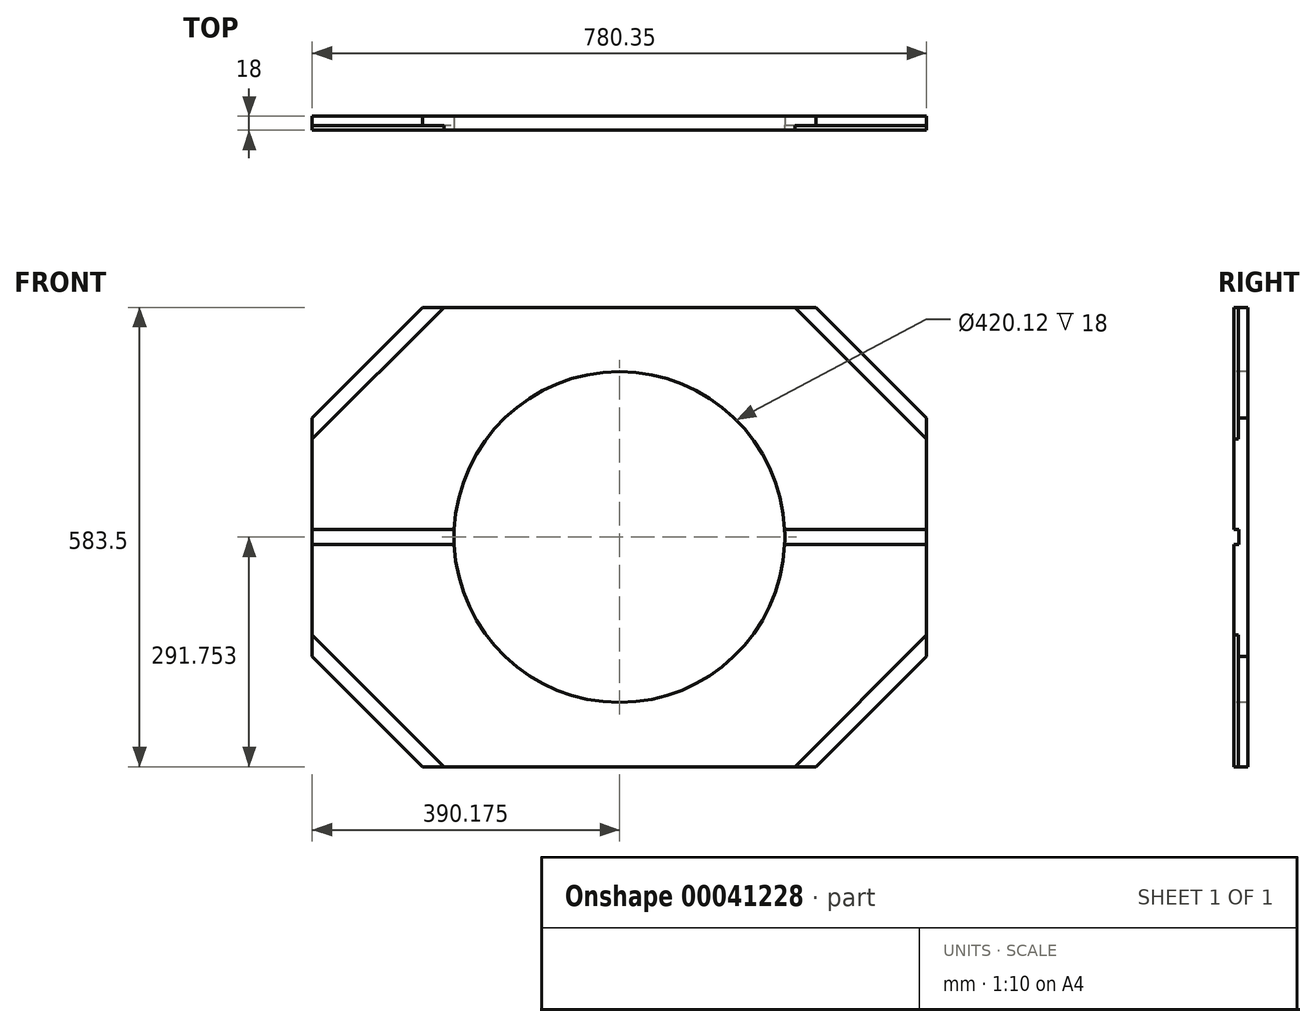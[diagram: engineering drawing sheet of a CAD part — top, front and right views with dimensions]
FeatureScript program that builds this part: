
annotation { "Feature Type Name" : "Feature", "Feature Type Description" : "" }
export const myFeature = defineFeature(function(context is Context, id is Id, definition is map)
    precondition{}
    {
        {
            var Q0;
            Q0=qCreatedBy(makeId("Front.planeOp"),FACE);
            var sketch = newSketch(context, id + "F0", { "sketchPlane" : qUnion([Q0])});
            skLineSegment(sketch, "E0.bottom", {"start": v(-320.85, 288.5) * mm, "end": v(459.5, 288.5) * mm});
            skLineSegment(sketch, "E0.top", {"start": v(-320.85, -295) * mm, "end": v(459.5, -295) * mm});
            skLineSegment(sketch, "E0.left", {"start": v(-320.85, 288.5) * mm, "end": v(-320.85, -295) * mm});
            skLineSegment(sketch, "E0.right", {"start": v(459.5, 288.5) * mm, "end": v(459.5, -295) * mm});
            skSolve(sketch);
        }
        {
            var Q0;
            Q0 = qSketchRegion(id + "F0", true);
            extrude(context, id + "F1", {"entities" : qUnion([Q0]), "depth" : 18 * mm});
        }
        {
            var Q0;
            Q0=makeQuery(id+"F1.opExtrude","CAP_FACE",FACE,{"disambiguationData":[OSD([sQuery(id+"F0.wireOp",EDGE,"E0.bottom"),sQuery(id+"F0.wireOp",EDGE,"E0.top"),sQuery(id+"F0.wireOp",EDGE,"E0.left"),sQuery(id+"F0.wireOp",EDGE,"E0.right")])],"isStart":false});
            var sketch = newSketch(context, id + "F2", { "sketchPlane" : qUnion([Q0])});
            skLineSegment(sketch, "E1", {"start": v(-320.85, -3.25) * mm, "end": v(459.5, -3.25) * mm, "construction": true});
            skLineSegment(sketch, "E2", {"start": v(69.32, -295) * mm, "end": v(69.32, 288.5) * mm, "construction": true});
            skPoint(sketch, "E3", {"position": v(69.32, -3.25) * mm});
            skSolve(sketch);
        }
        {
            var Q0;
            Q0=sQuery(id+"F2.wireOp",VERTEX,"E3");
            var Q1;
            Q1=makeQuery(id+"F1.opExtrude","SWEPT_BODY",BODY,{"disambiguationData":[OSD([sQuery(id+"F0.wireOp",EDGE,"E0.bottom"),sQuery(id+"F0.wireOp",EDGE,"E0.top"),sQuery(id+"F0.wireOp",EDGE,"E0.left"),sQuery(id+"F0.wireOp",EDGE,"E0.right")])]});
            hole(context, id + "F3", {"style" : HoleStyle.SIMPLE, "holeDiameter" : 420.12 * mm, "endStyle" : HoleEndStyle.THROUGH, "locations" : qUnion([Q0]), "scope" : qUnion([Q1])});
        }
        {
            var Q0;
            Q0=makeQuery(id+"F1.opExtrude","CAP_FACE",FACE,{"disambiguationData":[OSD([sQuery(id+"F0.wireOp",EDGE,"E0.bottom"),sQuery(id+"F0.wireOp",EDGE,"E0.top"),sQuery(id+"F0.wireOp",EDGE,"E0.left"),sQuery(id+"F0.wireOp",EDGE,"E0.right")])],"isStart":false});
            var sketch = newSketch(context, id + "F4", { "sketchPlane" : qUnion([Q0])});
            skLineSegment(sketch, "E4", {"start": v(-320.85, -154.63) * mm, "end": v(-180.48, -295) * mm});
            skLineSegment(sketch, "E5", {"start": v(-320.85, -154.63) * mm, "end": v(-320.85, -295) * mm});
            skLineSegment(sketch, "E6", {"start": v(-320.85, -295) * mm, "end": v(-180.48, -295) * mm});
            skLineSegment(sketch, "E7", {"start": v(-320.85, 148.14) * mm, "end": v(-180.49, 288.5) * mm});
            skLineSegment(sketch, "E8", {"start": v(-180.49, 288.5) * mm, "end": v(-320.85, 288.5) * mm});
            skLineSegment(sketch, "E9", {"start": v(-320.85, 288.5) * mm, "end": v(-320.85, 148.14) * mm});
            skLineSegment(sketch, "E10", {"start": v(459.5, 288.5) * mm, "end": v(459.5, 148.14) * mm});
            skLineSegment(sketch, "E11", {"start": v(459.5, 148.14) * mm, "end": v(319.14, 288.5) * mm});
            skLineSegment(sketch, "E12", {"start": v(319.14, 288.5) * mm, "end": v(459.5, 288.5) * mm});
            skLineSegment(sketch, "E13", {"start": v(459.5, -154.64) * mm, "end": v(319.14, -295) * mm});
            skLineSegment(sketch, "E14", {"start": v(319.14, -295) * mm, "end": v(459.5, -295) * mm});
            skLineSegment(sketch, "E15", {"start": v(459.5, -295) * mm, "end": v(459.5, -154.64) * mm});
            skSolve(sketch);
        }
        {
            var Q0;
            Q0 = qSketchRegion(id + "F4", true);
            extrude(context, id + "F5", {"entities" : qUnion([Q0]), "operationType" : NewBodyOperationType.REMOVE, "endBound" : BoundingType.THROUGH_ALL, "oppositeDirection" : true, "depth" : 25.4 * mm});
        }
        {
            var Q0;
            Q0=makeQuery(id+"F1.opExtrude","CAP_FACE",FACE,{"disambiguationData":[OSD([sQuery(id+"F0.wireOp",EDGE,"E0.bottom"),sQuery(id+"F0.wireOp",EDGE,"E0.top"),sQuery(id+"F0.wireOp",EDGE,"E0.left"),sQuery(id+"F0.wireOp",EDGE,"E0.right")])],"isStart":false});
            var sketch = newSketch(context, id + "F6", { "sketchPlane" : qUnion([Q0])});
            skLineSegment(sketch, "E16", {"start": v(-320.85, -154.63) * mm, "end": v(-320.85, -127.76) * mm});
            skLineSegment(sketch, "E17", {"start": v(-320.85, -127.76) * mm, "end": v(-153.61, -295) * mm});
            skLineSegment(sketch, "E18", {"start": v(-153.61, -295) * mm, "end": v(-180.48, -295) * mm});
            skLineSegment(sketch, "E19", {"start": v(-180.48, -295) * mm, "end": v(-320.85, -154.63) * mm});
            skLineSegment(sketch, "E20", {"start": v(69.32, 288.5) * mm, "end": v(69.32, -295) * mm, "construction": true});
            skLineSegment(sketch, "E21", {"start": v(-320.85, -3.24) * mm, "end": v(459.5, -3.24) * mm, "construction": true});
            skLineSegment(sketch, "E22.MirrorCS", {"start": v(319.13, -295) * mm, "end": v(459.5, -154.63) * mm});
            skLineSegment(sketch, "E23.MirrorCS", {"start": v(459.5, -154.63) * mm, "end": v(459.5, -127.76) * mm});
            skLineSegment(sketch, "E24.MirrorCS", {"start": v(459.5, -127.76) * mm, "end": v(292.26, -295) * mm});
            skLineSegment(sketch, "E25.MirrorCS", {"start": v(292.26, -295) * mm, "end": v(319.13, -295) * mm});
            skLineSegment(sketch, "E26.MirrorCS", {"start": v(292.26, 288.5) * mm, "end": v(319.13, 288.5) * mm});
            skLineSegment(sketch, "E27.MirrorCS", {"start": v(459.5, 148.14) * mm, "end": v(459.5, 121.27) * mm});
            skLineSegment(sketch, "E28.MirrorCS", {"start": v(459.5, 121.27) * mm, "end": v(292.26, 288.5) * mm});
            skLineSegment(sketch, "E29.MirrorCS", {"start": v(-153.61, 288.5) * mm, "end": v(-180.48, 288.5) * mm});
            skLineSegment(sketch, "E30.MirrorCS", {"start": v(-320.85, 121.27) * mm, "end": v(-153.61, 288.5) * mm});
            skLineSegment(sketch, "E31.MirrorCS", {"start": v(-180.48, 288.5) * mm, "end": v(-320.85, 148.14) * mm});
            skLineSegment(sketch, "E32.MirrorCS", {"start": v(-320.85, 148.14) * mm, "end": v(-320.85, 121.27) * mm});
            skLineSegment(sketch, "E33.MirrorCS", {"start": v(319.13, 288.5) * mm, "end": v(459.5, 148.14) * mm});
            skSolve(sketch);
        }
        {
            var Q0;
            Q0 = qSketchRegion(id + "F6", true);
            extrude(context, id + "F7", {"entities" : qUnion([Q0]), "operationType" : NewBodyOperationType.REMOVE, "oppositeDirection" : true, "depth" : 6 * mm});
        }
        {
            var Q0;
            Q0=makeQuery(id+"F1.opExtrude","CAP_FACE",FACE,{"disambiguationData":[OSD([sQuery(id+"F0.wireOp",EDGE,"E0.bottom"),sQuery(id+"F0.wireOp",EDGE,"E0.top"),sQuery(id+"F0.wireOp",EDGE,"E0.left"),sQuery(id+"F0.wireOp",EDGE,"E0.right")])],"isStart":false});
            var sketch = newSketch(context, id + "F8", { "sketchPlane" : qUnion([Q0])});
            skLineSegment(sketch, "E34", {"start": v(-320.85, -3.24) * mm, "end": v(459.5, -3.24) * mm, "construction": true});
            skLineSegment(sketch, "E35.bottom", {"start": v(-333.4, 6.26) * mm, "end": v(495.23, 6.26) * mm});
            skLineSegment(sketch, "E35.top", {"start": v(-333.4, -12.74) * mm, "end": v(495.23, -12.74) * mm});
            skLineSegment(sketch, "E35.left", {"start": v(-333.4, 6.26) * mm, "end": v(-333.4, -12.74) * mm});
            skLineSegment(sketch, "E35.right", {"start": v(495.23, 6.26) * mm, "end": v(495.23, -12.74) * mm});
            skSolve(sketch);
        }
        {
            var Q0;
            Q0 = qSketchRegion(id + "F8", true);
            extrude(context, id + "F9", {"entities" : qUnion([Q0]), "operationType" : NewBodyOperationType.REMOVE, "oppositeDirection" : true, "depth" : 6.5 * mm});
        }
    });
